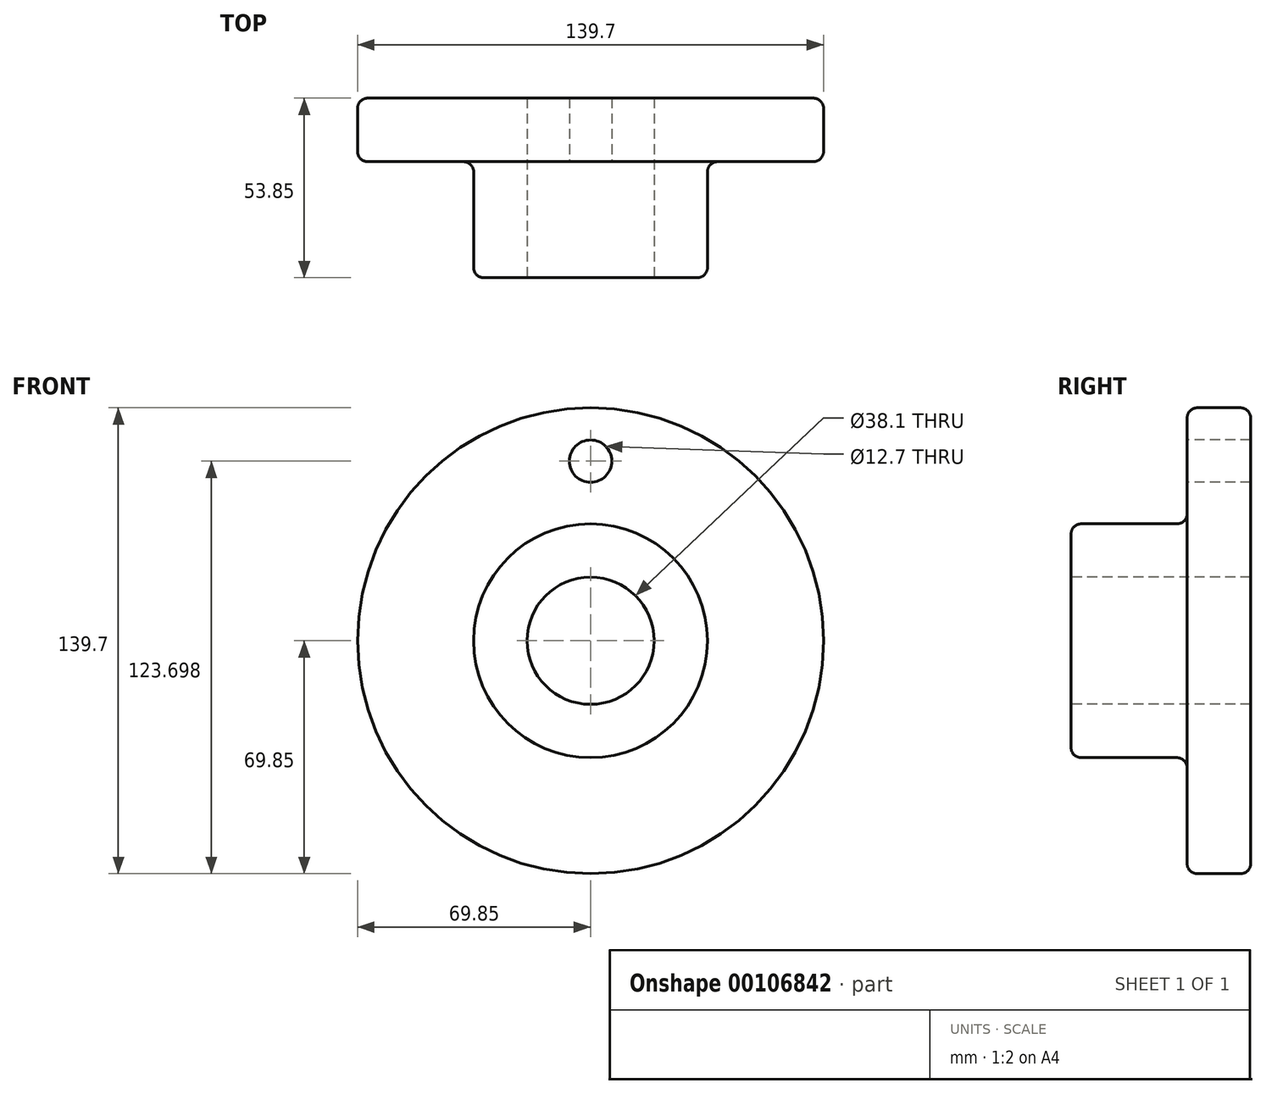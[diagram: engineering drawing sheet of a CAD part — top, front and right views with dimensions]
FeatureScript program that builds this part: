
annotation { "Feature Type Name" : "Feature", "Feature Type Description" : "" }
export const myFeature = defineFeature(function(context is Context, id is Id, definition is map)
    precondition{}
    {
        {
            var Q0;
            Q0=qCreatedBy(makeId("Right.planeOp"),FACE);
            var sketch = newSketch(context, id + "F0", { "sketchPlane" : qUnion([Q0])});
            skLineSegment(sketch, "E0.bottom", {"start": v(0, 69.85) * mm, "end": v(19.05, 69.85) * mm});
            skLineSegment(sketch, "E0.top", {"start": v(0, 19.05) * mm, "end": v(19.05, 19.05) * mm});
            skLineSegment(sketch, "E0.left", {"start": v(0, 69.85) * mm, "end": v(0, 19.05) * mm});
            skLineSegment(sketch, "E0.right", {"start": v(19.05, 69.85) * mm, "end": v(19.05, 19.05) * mm});
            skLineSegment(sketch, "E1", {"start": v(0, 0) * mm, "end": v(49.66, 0) * mm, "construction": true});
            skSolve(sketch);
        }
        {
            var Q0;
            Q0=makeQuery(id+"F0.imprint","IMPRINT",FACE,{"disambiguationData":[TD([[makeQuery(id+"F0.imprint","IMPRINT",EDGE,{"derivedFrom":sQuery(id+"F0.wireOp",EDGE,"E0.bottom")}),-1.0]])]});
            var Q1;
            Q1=sQuery(id+"F0.wireOp",EDGE,"E1");
            revolve(context, id + "F1", {"entities" : qUnion([Q0]), "axis" : qUnion([Q1]), "revolveType" : RevolveType.FULL});
        }
        {
            var Q0;
            Q0=makeQuery(id+"F1.opRevolve","SWEPT_FACE",FACE,{"disambiguationData":[OSD([sQuery(id+"F0.wireOp",EDGE,"E0.left")])]});
            var sketch = newSketch(context, id + "F2", { "sketchPlane" : qUnion([Q0])});
            skCircle(sketch, "E2", {"center": v(0, 0) * mm, "radius": 35.05 * mm});
            skCircle(sketch, "E3", {"center": v(0, 0) * mm, "radius": 53.85 * mm, "construction": true});
            skCircle(sketch, "E4", {"center": v(0, 53.85) * mm, "radius": 6.35 * mm});
            skSolve(sketch);
        }
        {
            var Q0;
            Q0=makeQuery(id+"F2.imprint","IMPRINT",FACE,{"disambiguationData":[TD([[makeQuery(id+"F2.imprint","IMPRINT",EDGE,{"derivedFrom":sQuery(id+"F2.wireOp",EDGE,"E2")}),1.0]])]});
            extrude(context, id + "F3", {"entities" : qUnion([Q0]), "operationType" : NewBodyOperationType.ADD, "depth" : 34.8 * mm});
        }
        {
            var Q0;
            Q0=makeQuery(id+"F2.imprint","IMPRINT",FACE,{"disambiguationData":[TD([[makeQuery(id+"F2.imprint","IMPRINT",EDGE,{"derivedFrom":sQuery(id+"F2.wireOp",EDGE,"E4")}),1.0]])]});
            extrude(context, id + "F4", {"entities" : qUnion([Q0]), "operationType" : NewBodyOperationType.REMOVE, "endBound" : BoundingType.THROUGH_ALL, "oppositeDirection" : true, "depth" : 25.4 * mm});
        }
        {
            var Q0;
            Q0=makeQuery(id+"F1.opRevolve","SWEPT_EDGE",EDGE,{"disambiguationData":[OSD([sQuery(id+"F0.wireOp",EDGE,"E0.bottom"),sQuery(id+"F0.wireOp",EDGE,"E0.left")])]});
            var Q1;
            Q1=makeQuery(id+"F1.opRevolve","SWEPT_EDGE",EDGE,{"disambiguationData":[OSD([sQuery(id+"F0.wireOp",EDGE,"E0.bottom"),sQuery(id+"F0.wireOp",EDGE,"E0.right")])]});
            fillet(context, id + "F5", {"entities" : qUnion([Q0, Q1]), "radius" : 3.05 * mm, "tangentPropagation" : true, "allowEdgeOverflow" : false});
        }
        {
            var Q0;
            Q0=makeQuery(id+"F3.opExtrude","SWEPT_FACE",FACE,{"disambiguationData":[OSD([sQuery(id+"F2.wireOp",EDGE,"E2")])]});
            fillet(context, id + "F6", {"entities" : qUnion([Q0]), "radius" : 3.05 * mm, "tangentPropagation" : true, "allowEdgeOverflow" : false});
        }
    });
